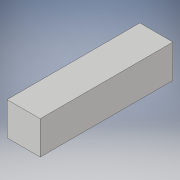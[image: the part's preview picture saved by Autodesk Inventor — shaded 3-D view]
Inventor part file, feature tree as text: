
AUTODESK INVENTOR PART (.ipt)
format: ipt  version: 2017 (Build 210142000, 142)  size: 86,528 bytes
history: native  units: in
note: dims shown in document units (in); Inventor stores cm internally (conversion verified against a paired STEP export)
features: extrude x1, sketch x1
ambient origin geometry x8: Origin, YZ Plane, XZ Plane, XY Plane, X Axis, Y Axis, Z Axis, Center Point
bodies: Solid1 (feature_tree)
feature tree (2):
  extrude  "Extrusion1"  Depth=0.125in
  sketch  "Sketch1"  dims[d0=0.125in d1=0.125in d2=0.5in d3=0.0in]
